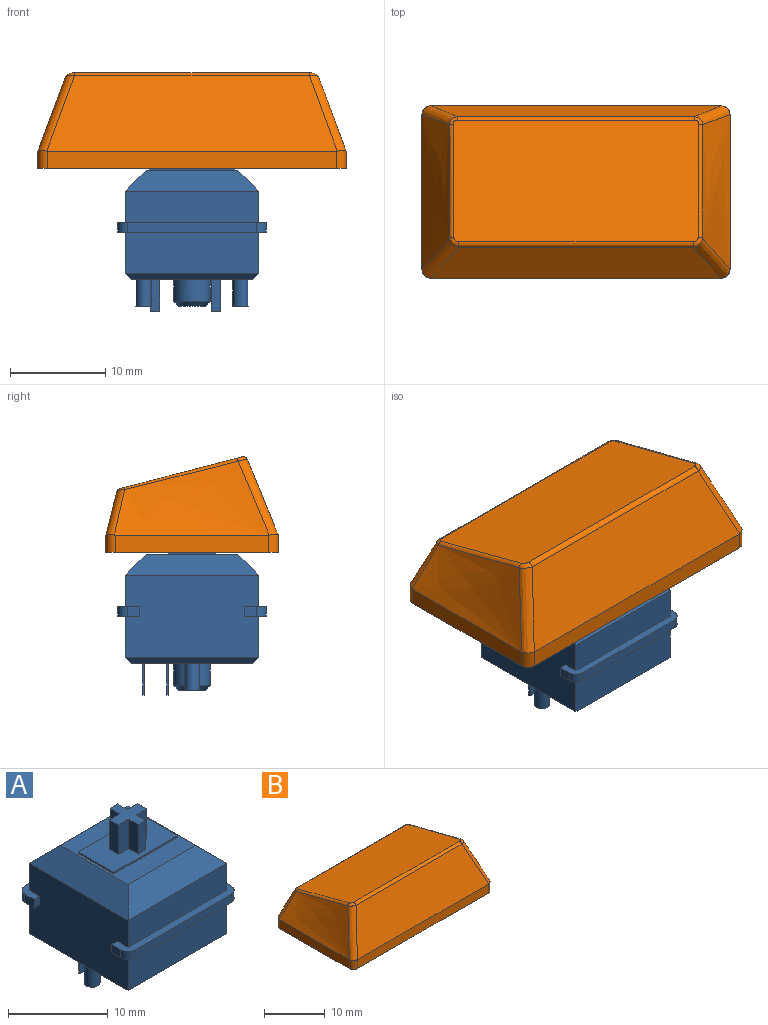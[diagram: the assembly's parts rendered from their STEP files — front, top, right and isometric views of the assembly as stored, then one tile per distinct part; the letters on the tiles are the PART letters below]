
ASSEMBLY  parts=2 mates=1
PART A: 69 faces, bbox 15.6x15.6x18.6 mm
  f0: plane 15.6x2.3mm, normal (0,0,-1), area 14.4mm2, adj f2,f3,f28,f30,f35,f60,f62,f63
  f1: plane 15.6x2.3mm, normal (0,0,-1), area 14.4mm2, adj f28,f30,f33,f34,f36,f59,f61,f64
  f2: plane 1.3x1mm, normal (1,0,0), area 1.3mm2, adj f0,f32,f62,f66
  f3: plane 1.3x1mm, normal (-1,0,0), area 1.3mm2, adj f0,f32,f63,f68
  f4: plane 15.6x2.3mm, normal (0,0,1), area 14.4mm2, adj f28,f30,f31,f33,f34,f36,f61,f64
  f5: plane 14x2.2mm, normal (-0.71,0,0.71), area 36.7mm2, adj f6,f7,f26,f30
  f6: plane 14x2.2mm, normal (0,-0.71,0.71), area 36.7mm2, adj f5,f7,f27,f31
  f7: plane 9.6x9.6mm, normal (0,0,1), area 47.2mm2, adj f5,f6,f8,f9,f10,f11,f26,f27
  f8: plane 5x0.2mm, normal (1,0,0), area 1mm2, adj f7,f9,f11,f12
  f9: plane 9x0.2mm, normal (0,1,0), area 1.8mm2, adj f7,f8,f10,f12
  f10: plane 5x0.2mm, normal (-1,0,0), area 1mm2, adj f7,f9,f11,f12
  f11: plane 9x0.2mm, normal (0,-1,0), area 1.8mm2, adj f7,f8,f10,f12
  f12: plane 9x5mm, normal (0,0,1), area 36.9mm2, adj f8,f9,f10,f11,f13,f14,f15,f16
  f13: plane 3.6x1.35mm, normal (1,0,0), area 4.9mm2, adj f12,f14,f24,f25
  f14: plane 3.6x1.08mm, normal (0,1,0), area 3.9mm2, adj f12,f13,f15,f25
  f15: plane 3.6x1.35mm, normal (-1,0,0), area 4.9mm2, adj f12,f14,f16,f25
  f16: plane 3.6x1.46mm, normal (0,1,0), area 5.3mm2, adj f12,f15,f17,f25
  f17: plane 3.6x1.3mm, normal (-1,0,0), area 4.7mm2, adj f12,f16,f18,f25
  f18: plane 3.6x1.46mm, normal (0,-1,0), area 5.3mm2, adj f12,f17,f19,f25
  f19: plane 3.6x1.35mm, normal (-1,0,0), area 4.9mm2, adj f12,f18,f20,f25
  f20: plane 3.6x1.08mm, normal (0,-1,0), area 3.9mm2, adj f12,f19,f21,f25
  f21: plane 3.6x1.35mm, normal (1,0,0), area 4.9mm2, adj f12,f20,f22,f25
  f22: plane 3.6x1.46mm, normal (0,-1,0), area 5.3mm2, adj f12,f21,f23,f25
  f23: plane 3.6x1.3mm, normal (1,0,0), area 4.7mm2, adj f12,f22,f24,f25
  f24: plane 3.6x1.46mm, normal (0,1,0), area 5.3mm2, adj f12,f13,f23,f25
  f25: plane 4x4mm, normal (0,0,1), area 8.1mm2, adj f13,f14,f15,f16,f17,f18,f19,f20
  f26: plane 14x2.2mm, normal (0,0.71,0.71), area 36.7mm2, adj f5,f7,f27,f29
  f27: plane 14x2.2mm, normal (0.71,0,0.71), area 36.7mm2, adj f6,f7,f26,f28
  f28: plane 14x8.6mm, normal (1,0,0), area 117.4mm2, adj f0,f1,f4,f27,f29,f31,f32,f55
  f29: plane 14x3.3mm, normal (0,1,0), area 46.2mm2, adj f26,f28,f30,f32
  f30: plane 14x8.6mm, normal (-1,0,0), area 117.4mm2, adj f0,f1,f4,f5,f29,f31,f32,f57
  f31: plane 14x3.3mm, normal (0,-1,0), area 46.2mm2, adj f4,f6,f28,f30
  f32: plane 15.6x2.3mm, normal (0,0,1), area 14.4mm2, adj f2,f3,f28,f29,f30,f35,f62,f63
  f33: plane 13.6x1mm, normal (0,-1,0), area 13.6mm2, adj f1,f4,f61,f64
  f34: plane 1.3x1mm, normal (1,0,0), area 1.3mm2, adj f1,f4,f61,f65
  f35: plane 13.6x1mm, normal (0,1,0), area 13.6mm2, adj f0,f32,f62,f63
  f36: plane 1.3x1mm, normal (-1,0,0), area 1.3mm2, adj f1,f4,f64,f67
  f37: plane 2.85x2.85mm, normal (0,0,-1), area 6.4mm2, adj f38
  f38: cone r=1.43mm half-angle=45deg, axis (0,0,1), area 7.4mm2, adj f37,f43
  f39: plane 1x0.2mm, normal (0,0,-1), area 0.2mm2, adj f44,f45,f46,f47
  f40: plane 1x0.2mm, normal (0,0,-1), area 0.2mm2, adj f48,f49,f50,f51
  f41: plane 1.6x1.6mm, normal (0,0,-1), area 2mm2, adj f52
  f42: plane 1.6x1.6mm, normal (0,0,-1), area 2mm2, adj f53
  f43: cylinder r=1.93mm len=3.85mm, axis (0,0,1), area 27.8mm2, adj f38,f54
  f44: plane 3.3x0.2mm, normal (-1,0,0), area 0.7mm2, adj f39,f45,f47,f54
  f45: plane 3.3x1mm, normal (0,1,0), area 3.3mm2, adj f39,f44,f46,f54
  f46: plane 3.3x0.2mm, normal (1,0,0), area 0.7mm2, adj f39,f45,f47,f54
  f47: plane 3.3x1mm, normal (0,-1,0), area 3.3mm2, adj f39,f44,f46,f54
  f48: plane 3.3x0.2mm, normal (-1,0,0), area 0.7mm2, adj f40,f49,f51,f54
  f49: plane 3.3x1mm, normal (0,1,0), area 3.3mm2, adj f40,f48,f50,f54
  f50: plane 3.3x0.2mm, normal (1,0,0), area 0.7mm2, adj f40,f49,f51,f54
  f51: plane 3.3x1mm, normal (0,-1,0), area 3.3mm2, adj f40,f48,f50,f54
  f52: cylinder r=0.8mm len=2.8mm, axis (0,0,1), area 14.1mm2, adj f41,f54
  f53: cylinder r=0.8mm len=2.8mm, axis (0,0,1), area 14.1mm2, adj f42,f54
  f54: plane 12.6x12.6mm, normal (0,0,-1), area 142.7mm2, adj f43,f44,f45,f46,f47,f48,f49,f50
  f55: plane 14x0.7mm, normal (0.71,0,-0.71), area 13.2mm2, adj f28,f54,f56,f58
  f56: plane 14x0.7mm, normal (0,0.71,-0.71), area 13.2mm2, adj f54,f55,f57,f60
  f57: plane 14x0.7mm, normal (-0.71,0,-0.71), area 13.2mm2, adj f30,f54,f56,f58
  f58: plane 14x0.7mm, normal (0,-0.71,-0.71), area 13.2mm2, adj f54,f55,f57,f59
  f59: plane 14x4.3mm, normal (0,-1,0), area 60.2mm2, adj f1,f28,f30,f58
  f60: plane 14x4.3mm, normal (0,1,0), area 60.2mm2, adj f0,f28,f30,f56
  f61: cylinder r=1mm len=1mm, axis (0,0,-1), area 1.6mm2, adj f1,f4,f33,f34
  f62: cylinder r=1mm len=1mm, axis (0,0,1), area 1.6mm2, adj f0,f2,f32,f35
  f63: cylinder r=1mm len=1mm, axis (0,0,-1), area 1.6mm2, adj f0,f3,f32,f35
  f64: cylinder r=1mm len=1mm, axis (0,0,1), area 1.6mm2, adj f1,f4,f33,f36
  f65: plane 1x0.8mm, normal (0,1,0), area 0.8mm2, adj f1,f4,f28,f34
  f66: plane 1x0.8mm, normal (0,-1,0), area 0.8mm2, adj f0,f2,f28,f32
  f67: plane 1x0.8mm, normal (0,1,0), area 0.8mm2, adj f1,f4,f30,f36
  f68: plane 1x0.8mm, normal (0,-1,0), area 0.8mm2, adj f0,f3,f30,f32
PART B: 50 faces, bbox 36.6x22.7x14.6 mm
  f0: plane 32.35x18.1mm, normal (0,0,-1), area 96mm2, adj f1,f2,f3,f4,f10,f12,f14,f16
  f1: plane 30.35x1.8mm, normal (0,-1,0), area 54.6mm2, adj f0,f8,f10,f12
  f2: plane 16.1x1.8mm, normal (1,0,0), area 29mm2, adj f0,f9,f10,f16
  f3: plane 30.35x1.8mm, normal (0,1,0), area 54.6mm2, adj f0,f6,f14,f15,f16,f17
  f4: plane 16.1x1.8mm, normal (-1,0,0), area 29mm2, adj f0,f7,f12,f14
  f5: plane 25.81x12.77mm, normal (0,0.25,0.97), area 338.9mm2, adj f18,f19,f20,f21,f22,f23,f24,f25
  f6: plane 30.31x4.53mm, normal (0,0.97,0.25), area 129mm2, adj f3,f15,f17,f20
  f7: bspline ~18.1x8.31mm, area 98.6mm2, adj f4,f12,f13,f14,f15,f19
  f8: plane 30.5x7.9mm, normal (0,-0.93,0.38), area 235.3mm2, adj f1,f10,f11,f12,f13,f23
  f9: bspline ~18.1x8.31mm, area 98.6mm2, adj f2,f10,f11,f16,f17,f24
  f10: cylinder r=1mm len=1.87mm, axis (0,0,1), area 2.9mm2, adj f0,f1,f2,f8,f9,f11
  f11: bspline ~11.3x5.51mm, area 13.2mm2, adj f8,f9,f10,f25
  f12: cylinder r=1mm len=1.87mm, axis (0,0,-1), area 2.9mm2, adj f0,f1,f4,f7,f8,f13
  f13: bspline ~11.44x5.57mm, area 13.2mm2, adj f7,f8,f12,f21
  f14: cylinder r=1mm len=1.81mm, axis (0,0,1), area 2.8mm2, adj f0,f3,f4,f7,f15
  f15: bspline ~7.23x4.95mm, area 7.7mm2, adj f3,f6,f7,f14,f18
  f16: cylinder r=1mm len=1.81mm, axis (0,0,-1), area 2.8mm2, adj f0,f2,f3,f9,f17
  f17: bspline ~7.14x4.9mm, area 7.7mm2, adj f3,f6,f9,f16,f22
  f18: bspline ~1.16x0.9mm, area 0.5mm2, adj f5,f15,f19,f20
  f19: bspline ~18.2x4.87mm, area 7mm2, adj f5,f7,f18,f21
  f20: cylinder r=0.5mm len=24.93mm, axis (-1,0,0), area 13.3mm2, adj f5,f6,f18,f22
  f21: bspline ~1.24x1.04mm, area 0.8mm2, adj f5,f13,f19,f23
  f22: bspline ~1.09x0.94mm, area 0.5mm2, adj f5,f17,f20,f24
  f23: cylinder r=0.5mm len=24.63mm, axis (-1,0,0), area 17.7mm2, adj f5,f8,f21,f25
  f24: bspline ~15.84x4.3mm, area 7mm2, adj f5,f9,f22,f25
  f25: bspline ~1.22x1.1mm, area 0.8mm2, adj f5,f11,f23,f24
  f26: plane 30.35x1.61mm, normal (0,1,0), area 48.7mm2, adj f0,f27,f29,f33
  f27: plane 16.18x1.7mm, normal (-1,0,0), area 25.3mm2, adj f0,f26,f28,f34
  f28: plane 30.35x1.67mm, normal (0,-1,0), area 50.8mm2, adj f0,f27,f29,f31,f32,f34
  f29: plane 16.18x1.7mm, normal (1,0,0), area 25.3mm2, adj f0,f26,f28,f32
  f30: plane 28.12x14.91mm, normal (0,-0.25,-0.97), area 287.8mm2, adj f31,f32,f33,f34,f45
  f31: plane 30.18x4.13mm, normal (0,-0.97,-0.25), area 117.8mm2, adj f28,f30,f32,f34
  f32: offset ~20.1x10.31mm, area 90.9mm2, adj f28,f29,f30,f31,f33
  f33: plane 30.4x7.36mm, normal (0,0.93,-0.38), area 218.5mm2, adj f26,f30,f32,f34
  f34: offset ~20.1x10.31mm, area 90.8mm2, adj f27,f28,f30,f31,f33
  f35: plane 7.44x1.35mm, normal (-1,0,0), area 9.8mm2, adj f36,f44,f47,f49
  f36: plane 7.44x1.5mm, normal (0,-1,0), area 11.2mm2, adj f35,f37,f44,f49
  f37: plane 7.77x1.3mm, normal (-1,0,0), area 9.9mm2, adj f36,f38,f44,f49
  f38: plane 7.77x1.5mm, normal (0,1,0), area 11.7mm2, adj f37,f39,f44,f49
  f39: plane 8.12x1.35mm, normal (-1,0,0), area 10.7mm2, adj f38,f40,f44,f49
  f40: plane 8.12x1mm, normal (0,1,0), area 8.1mm2, adj f39,f41,f44,f49
  f41: plane 8.12x1.35mm, normal (1,0,0), area 10.7mm2, adj f40,f42,f44,f49
  f42: plane 7.77x1.5mm, normal (0,1,0), area 11.7mm2, adj f41,f43,f44,f49
  f43: plane 7.77x1.3mm, normal (1,0,0), area 9.9mm2, adj f42,f44,f46,f49
  f44: plane 5.5x5.5mm, normal (0,0,-1), area 15.9mm2, adj f35,f36,f37,f38,f39,f40,f41,f42
  f45: cylinder r=2.75mm len=6.89mm, axis (0,0,-1), area 119.1mm2, adj f30,f44
  f46: plane 7.44x1.5mm, normal (0,-1,0), area 11.2mm2, adj f43,f44,f48,f49
  f47: plane 7.09x1mm, normal (0,-1,0), area 7.1mm2, adj f35,f44,f48,f49
  f48: plane 7.44x1.35mm, normal (1,0,0), area 9.8mm2, adj f44,f46,f47,f49
  f49: plane 4x4mm, normal (0,-0.25,-0.97), area 8.2mm2, adj f35,f36,f37,f38,f39,f40,f41,f42
PLACE A at identity fixed
PLACE B t=(0,0,11.7)mm
MATE fastened B.f45 <-> A.f38  axis (0,0,-1) through (0,0,11.7)mm
